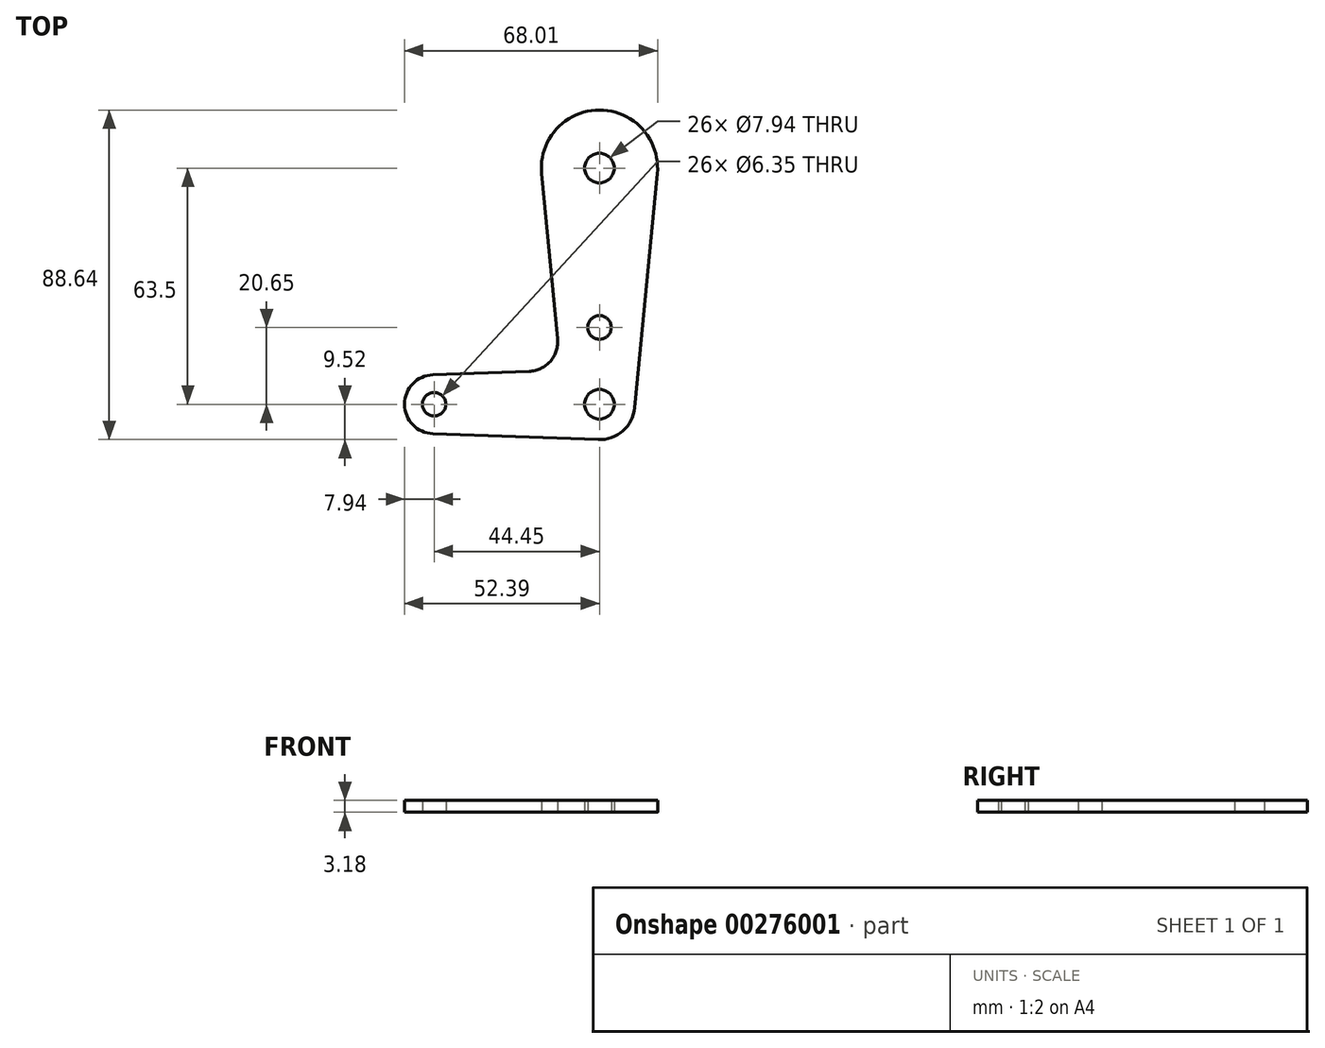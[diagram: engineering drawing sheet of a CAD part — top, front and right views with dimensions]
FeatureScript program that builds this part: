
annotation { "Feature Type Name" : "Feature", "Feature Type Description" : "" }
export const myFeature = defineFeature(function(context is Context, id is Id, definition is map)
    precondition{}
    {
        {
            var Q0;
            Q0=qCreatedBy(makeId("Top.planeOp"),FACE);
            var sketch = newSketch(context, id + "F0", { "sketchPlane" : qUnion([Q0])});
            skCircle(sketch, "E0", {"center": v(0, 0) * mm, "radius": 3.97 * mm});
            skLineSegment(sketch, "E1", {"start": v(0, 0) * mm, "end": v(-44.45, 0) * mm, "construction": true});
            skCircle(sketch, "E2", {"center": v(-44.45, 0) * mm, "radius": 3.18 * mm});
            skCircle(sketch, "E3", {"center": v(-44.45, 0) * mm, "radius": 7.94 * mm});
            skLineSegment(sketch, "E4", {"start": v(0, 0) * mm, "end": v(0, 63.5) * mm, "construction": true});
            skCircle(sketch, "E5", {"center": v(0, 63.5) * mm, "radius": 3.97 * mm});
            skCircle(sketch, "E6", {"center": v(0, 63.5) * mm, "radius": 15.62 * mm});
            skCircle(sketch, "E7", {"center": v(0, 0) * mm, "radius": 9.53 * mm});
            skLineSegment(sketch, "E8", {"start": v(0, 0) * mm, "end": v(0, 20.65) * mm, "construction": true});
            skCircle(sketch, "E9", {"center": v(0, 20.65) * mm, "radius": 3.18 * mm});
            skLineSegment(sketch, "E10", {"start": v(15.55, 62) * mm, "end": v(9.48, -0.91) * mm});
            skLineSegment(sketch, "E11", {"start": v(-15.55, 62) * mm, "end": v(-9.48, -0.91) * mm});
            skLineSegment(sketch, "E12", {"start": v(-44.73, 7.93) * mm, "end": v(0, 9.53) * mm});
            skLineSegment(sketch, "E13", {"start": v(-44.73, -7.93) * mm, "end": v(-0.34, -9.52) * mm});
            skSolve(sketch);
        }
        {
            var Q0;
            Q0=qSketchRegion(id+"F0",true);
            extrude(context, id + "F1", {"entities" : qUnion([Q0]), "depth" : 3.17 * mm});
        }
        {
            var Q0;
            Q0=makeQuery(id+"F1.opExtrude","SWEPT_EDGE",EDGE,{"disambiguationData":[OSD([sQuery(id+"F0.wireOp",EDGE,"E11"),sQuery(id+"F0.wireOp",EDGE,"E12")])]});
            fillet(context, id + "F2", {"entities" : qUnion([Q0]), "radius" : 7.94 * mm, "tangentPropagation" : true, "allowEdgeOverflow" : false});
        }
    });
